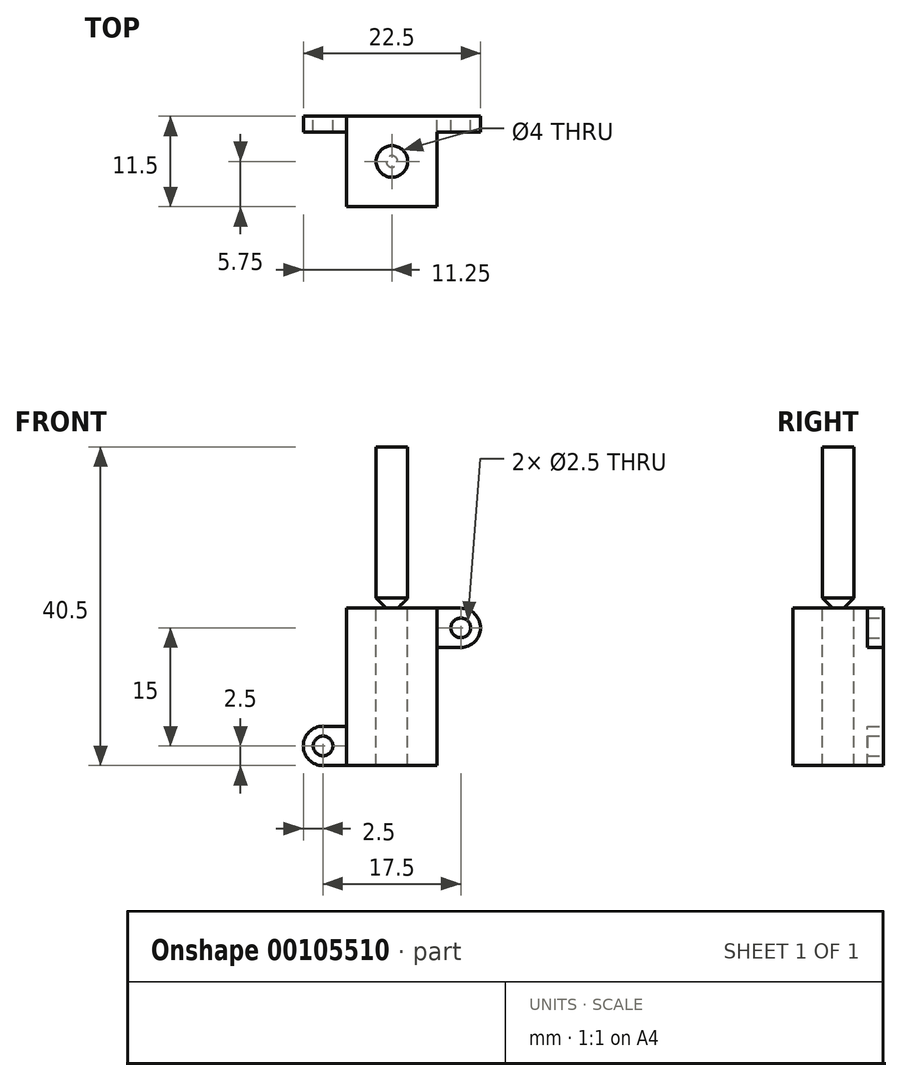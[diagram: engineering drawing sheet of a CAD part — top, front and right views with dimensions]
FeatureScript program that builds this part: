
annotation { "Feature Type Name" : "Feature", "Feature Type Description" : "" }
export const myFeature = defineFeature(function(context is Context, id is Id, definition is map)
    precondition{}
    {
        {
            var Q0;
            Q0=qCreatedBy(makeId("Front.planeOp"),FACE);
            var sketch = newSketch(context, id + "F0", { "sketchPlane" : qUnion([Q0])});
            skLineSegment(sketch, "E0.bottom", {"start": v(5.75, -10) * mm, "end": v(-5.75, -10) * mm});
            skLineSegment(sketch, "E0.top", {"start": v(5.75, 10) * mm, "end": v(-5.75, 10) * mm});
            skLineSegment(sketch, "E0.left", {"start": v(5.75, -10) * mm, "end": v(5.75, 10) * mm});
            skLineSegment(sketch, "E0.right", {"start": v(-5.75, -10) * mm, "end": v(-5.75, 10) * mm});
            skPoint(sketch, "E0.middle", {"position": v(0, 0) * mm});
            skSolve(sketch);
        }
        {
            var Q0;
            Q0=makeQuery(id+"F0.imprint","IMPRINT",FACE,{"disambiguationData":[TD([[makeQuery(id+"F0.imprint","IMPRINT",EDGE,{"derivedFrom":sQuery(id+"F0.wireOp",EDGE,"E0.bottom")}),-1.0]])]});
            extrude(context, id + "F1", {"entities" : qUnion([Q0]), "depth" : 11.5 * mm});
        }
        {
            var Q0;
            Q0=makeQuery(id+"F1.opExtrude","CAP_FACE",FACE,{"disambiguationData":[OSD([sQuery(id+"F0.wireOp",EDGE,"E0.bottom"),sQuery(id+"F0.wireOp",EDGE,"E0.top"),sQuery(id+"F0.wireOp",EDGE,"E0.left"),sQuery(id+"F0.wireOp",EDGE,"E0.right")])],"isStart":true});
            var sketch = newSketch(context, id + "F2", { "sketchPlane" : qUnion([Q0])});
            skLineSegment(sketch, "E1.bottom", {"start": v(-5.75, 10) * mm, "end": v(-8.75, 10) * mm});
            skLineSegment(sketch, "E1.top", {"start": v(-5.75, 5) * mm, "end": v(-8.75, 5) * mm});
            skLineSegment(sketch, "E1.left", {"start": v(-5.75, 10) * mm, "end": v(-5.75, 5) * mm});
            skLineSegment(sketch, "E1.right", {"start": v(-8.75, 10) * mm, "end": v(-8.75, 5) * mm, "construction": true});
            skLineSegment(sketch, "E2.bottom", {"start": v(5.75, -10) * mm, "end": v(8.75, -10) * mm});
            skLineSegment(sketch, "E2.top", {"start": v(5.75, -5) * mm, "end": v(8.75, -5) * mm});
            skLineSegment(sketch, "E2.left", {"start": v(5.75, -10) * mm, "end": v(5.75, -5) * mm});
            skLineSegment(sketch, "E2.right", {"start": v(8.75, -10) * mm, "end": v(8.75, -5) * mm, "construction": true});
            skArc(sketch, "E3", {"start": v(-8.75, 10) * mm, "mid": v(-11.25, 7.5) * mm, "end": v(-8.75, 5) * mm});
            skArc(sketch, "E4", {"start": v(8.75, -10) * mm, "mid": v(11.25, -7.5) * mm, "end": v(8.75, -5) * mm});
            skCircle(sketch, "E5", {"center": v(-8.75, 7.5) * mm, "radius": 1.25 * mm});
            skCircle(sketch, "E6", {"center": v(8.75, -7.5) * mm, "radius": 1.25 * mm});
            skSolve(sketch);
        }
        {
            var Q0;
            Q0=makeQuery(id+"F2.imprint","IMPRINT",FACE,{"disambiguationData":[TD([[makeQuery(id+"F2.imprint","IMPRINT",EDGE,{"derivedFrom":sQuery(id+"F2.wireOp",EDGE,"E1.bottom")}),1.0]])]});
            var Q1;
            Q1=makeQuery(id+"F2.imprint","IMPRINT",FACE,{"disambiguationData":[TD([[makeQuery(id+"F2.imprint","IMPRINT",EDGE,{"derivedFrom":sQuery(id+"F2.wireOp",EDGE,"E2.bottom")}),1.0]])]});
            extrude(context, id + "F3", {"entities" : qUnion([Q0, Q1]), "operationType" : NewBodyOperationType.ADD, "oppositeDirection" : true, "depth" : 2 * mm});
        }
        {
            var Q0;
            Q0=makeQuery(id+"F3.boolean.opBoolean","MERGE",FACE,{"derivedFrom":[makeQuery(id+"F1.opExtrude","SWEPT_FACE",FACE,{"disambiguationData":[OSD([sQuery(id+"F0.wireOp",EDGE,"E0.top")])]}),makeQuery(id+"F3.opExtrude","SWEPT_FACE",FACE,{"disambiguationData":[OSD([sQuery(id+"F2.wireOp",EDGE,"E1.bottom")])]})]});
            var sketch = newSketch(context, id + "F4", { "sketchPlane" : qUnion([Q0])});
            skCircle(sketch, "E7", {"center": v(0, -5.75) * mm, "radius": 2 * mm});
            skPoint(sketch, "E7.centerSnap0", {"position": v(0, -11.5) * mm});
            skPoint(sketch, "E7.centerSnap1", {"position": v(-5.75, -5.75) * mm});
            skSolve(sketch);
        }
        {
            var Q0;
            Q0 = qSketchRegion(id + "F4", true);
            extrude(context, id + "F5", {"entities" : qUnion([Q0]), "operationType" : NewBodyOperationType.REMOVE, "endBound" : BoundingType.THROUGH_ALL, "oppositeDirection" : true, "depth" : 25.4 * mm});
        }
        {
            var Q0;
            Q0=makeQuery(id+"F4.imprint","IMPRINT",FACE,{"disambiguationData":[TD([[makeQuery(id+"F4.imprint","IMPRINT",EDGE,{"derivedFrom":sQuery(id+"F4.wireOp",EDGE,"E7")}),1.0]])]});
            extrude(context, id + "F6", {"entities" : qUnion([Q0]), "depth" : 20.5 * mm});
        }
        {
            var Q0;
            Q0=makeQuery(id+"F6.opExtrude","CAP_EDGE",EDGE,{"disambiguationData":[OSD([sQuery(id+"F4.wireOp",EDGE,"E7")])],"isStart":true});
            chamfer(context, id + "F7", {"entities" : qUnion([Q0]), "chamferType" : ChamferType.OFFSET_ANGLE, "width" : 1.27 * mm, "oppositeDirection" : false, "angle" : 45 * degree, "tangentPropagation" : true});
        }
    });
